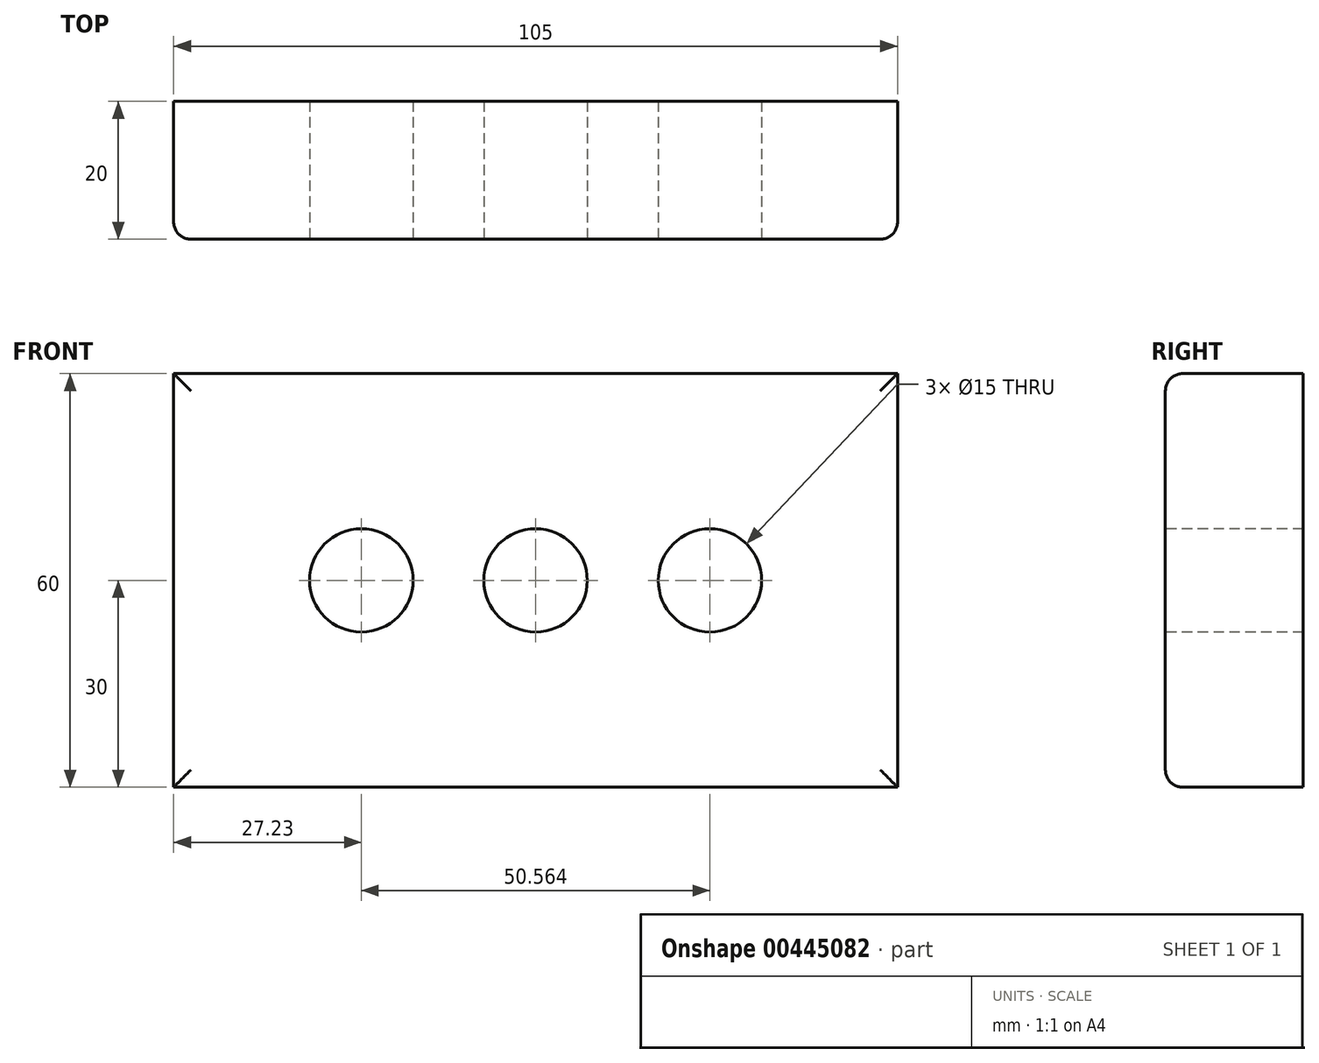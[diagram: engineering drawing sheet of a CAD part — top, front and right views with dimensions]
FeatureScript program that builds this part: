
annotation { "Feature Type Name" : "Feature", "Feature Type Description" : "" }
export const myFeature = defineFeature(function(context is Context, id is Id, definition is map)
    precondition{}
    {
        {
            var Q0;
            Q0=qCreatedBy(makeId("Front.planeOp"),FACE);
            var sketch = newSketch(context, id + "F0", { "sketchPlane" : qUnion([Q0])});
            skLineSegment(sketch, "E0.bottom", {"start": v(52.5, -30) * mm, "end": v(-52.5, -30) * mm});
            skLineSegment(sketch, "E0.top", {"start": v(52.5, 30) * mm, "end": v(-52.5, 30) * mm});
            skLineSegment(sketch, "E0.left", {"start": v(52.5, -30) * mm, "end": v(52.5, 30) * mm});
            skLineSegment(sketch, "E0.right", {"start": v(-52.5, -30) * mm, "end": v(-52.5, 30) * mm});
            skPoint(sketch, "E0.middle", {"position": v(0, 0) * mm});
            skSolve(sketch);
        }
        {
            var Q0;
            Q0 = qSketchRegion(id + "F0", true);
            var Q1;
            Q1=makeQuery(id+"F0.imprint","IMPRINT",FACE,{"disambiguationData":[TD([[makeQuery(id+"F0.imprint","IMPRINT",EDGE,{"derivedFrom":sQuery(id+"F0.wireOp",EDGE,"E0.bottom")}),-1.0]])]});
            extrude(context, id + "F1", {"entities" : qUnion([Q0, Q1]), "depth" : 20 * mm});
        }
        {
            var Q0;
            Q0=makeQuery(id+"F1.opExtrude","CAP_FACE",FACE,{"disambiguationData":[OSD([sQuery(id+"F0.wireOp",EDGE,"E0.bottom"),sQuery(id+"F0.wireOp",EDGE,"E0.top"),sQuery(id+"F0.wireOp",EDGE,"E0.left"),sQuery(id+"F0.wireOp",EDGE,"E0.right")])],"isStart":false});
            var sketch = newSketch(context, id + "F2", { "sketchPlane" : qUnion([Q0])});
            skCircle(sketch, "E1", {"center": v(0, 0) * mm, "radius": 7.5 * mm});
            skLineSegment(sketch, "E2", {"start": v(-7.5, 0) * mm, "end": v(-17.5, 0) * mm});
            skLineSegment(sketch, "E3", {"start": v(7.5, 0) * mm, "end": v(17.5, 0) * mm});
            skCircle(sketch, "E4", {"center": v(-25.27, 0) * mm, "radius": 7.5 * mm});
            skCircle(sketch, "E5", {"center": v(25.3, 0) * mm, "radius": 7.5 * mm});
            skSolve(sketch);
        }
        {
            var Q0;
            Q0=makeQuery(id+"F2.imprint","IMPRINT",FACE,{"disambiguationData":[TD([[makeQuery(id+"F2.imprint","IMPRINT",EDGE,{"derivedFrom":sQuery(id+"F2.wireOp",EDGE,"E1")}),1.0]])]});
            extrude(context, id + "F3", {"entities" : qUnion([Q0]), "operationType" : NewBodyOperationType.REMOVE, "oppositeDirection" : true, "depth" : 20 * mm});
        }
        {
            var Q0;
            Q0 = qSketchRegion(id + "F2", true);
            extrude(context, id + "F4", {"entities" : qUnion([Q0]), "operationType" : NewBodyOperationType.REMOVE, "oppositeDirection" : true, "depth" : 20 * mm});
        }
        {
            var Q0;
            Q0=makeQuery(id+"F1.opExtrude","CAP_EDGE",EDGE,{"disambiguationData":[OSD([sQuery(id+"F0.wireOp",EDGE,"E0.top")])],"isStart":false});
            var Q1;
            Q1=makeQuery(id+"F1.opExtrude","CAP_EDGE",EDGE,{"disambiguationData":[OSD([sQuery(id+"F0.wireOp",EDGE,"E0.right")])],"isStart":false});
            var Q2;
            Q2=makeQuery(id+"F1.opExtrude","CAP_EDGE",EDGE,{"disambiguationData":[OSD([sQuery(id+"F0.wireOp",EDGE,"E0.bottom")])],"isStart":false});
            var Q3;
            Q3=makeQuery(id+"F1.opExtrude","CAP_EDGE",EDGE,{"disambiguationData":[OSD([sQuery(id+"F0.wireOp",EDGE,"E0.left")])],"isStart":false});
            fillet(context, id + "F5", {"entities" : qUnion([Q0, Q1, Q2, Q3]), "radius" : 2.5 * mm, "tangentPropagation" : true, "allowEdgeOverflow" : false});
        }
    });
